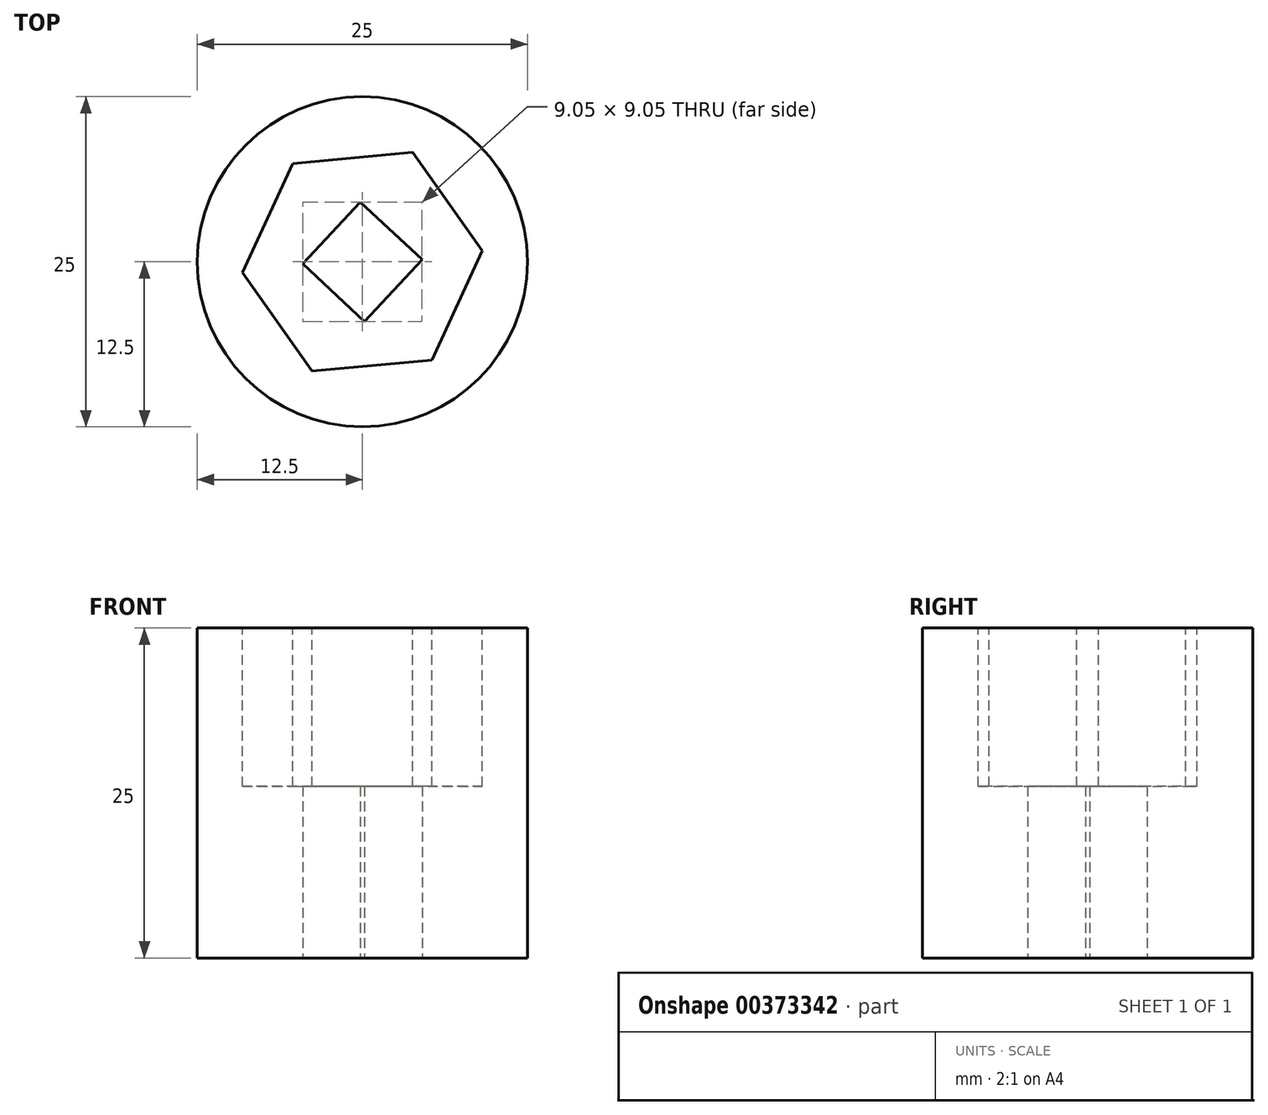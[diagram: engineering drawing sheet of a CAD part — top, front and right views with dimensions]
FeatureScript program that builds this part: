
annotation { "Feature Type Name" : "Feature", "Feature Type Description" : "" }
export const myFeature = defineFeature(function(context is Context, id is Id, definition is map)
    precondition{}
    {
        {
            var Q0;
            Q0=qCreatedBy(makeId("Top.planeOp"),FACE);
            var sketch = newSketch(context, id + "F0", { "sketchPlane" : qUnion([Q0])});
            skCircle(sketch, "E0", {"center": v(0, 0) * mm, "radius": 12.5 * mm});
            skSolve(sketch);
        }
        {
            var Q0;
            Q0=makeQuery(id+"F0.imprint","IMPRINT",FACE,{"disambiguationData":[TD([[makeQuery(id+"F0.imprint","IMPRINT",EDGE,{"derivedFrom":sQuery(id+"F0.wireOp",EDGE,"E0")}),1.0]])]});
            extrude(context, id + "F1", {"entities" : qUnion([Q0]), "depth" : 25 * mm});
        }
        {
            var Q0;
            Q0=makeQuery(id+"F1.opExtrude","CAP_FACE",FACE,{"disambiguationData":[OSD([sQuery(id+"F0.wireOp",EDGE,"E0")])],"isStart":false});
            var sketch = newSketch(context, id + "F2", { "sketchPlane" : qUnion([Q0])});
            skCircle(sketch, "E1.cCircle", {"center": v(0, 0) * mm, "radius": 7.9 * mm, "construction": true});
            skLineSegment(sketch, "E1.0", {"start": v(-3.82, -8.28) * mm, "end": v(-9.08, -0.83) * mm});
            skLineSegment(sketch, "E1.1", {"start": v(-9.08, -0.83) * mm, "end": v(-5.26, 7.45) * mm});
            skLineSegment(sketch, "E1.2", {"start": v(-5.26, 7.45) * mm, "end": v(3.82, 8.28) * mm});
            skLineSegment(sketch, "E1.3", {"start": v(3.82, 8.28) * mm, "end": v(9.08, 0.83) * mm});
            skLineSegment(sketch, "E1.4", {"start": v(9.08, 0.83) * mm, "end": v(5.26, -7.45) * mm});
            skLineSegment(sketch, "E1.5", {"start": v(5.26, -7.45) * mm, "end": v(-3.82, -8.28) * mm});
            skPoint(sketch, "E1.0.midPoint", {"position": v(-6.45, -4.56) * mm});
            skSolve(sketch);
        }
        {
            var Q0;
            Q0 = qSketchRegion(id + "F2", true);
            extrude(context, id + "F3", {"entities" : qUnion([Q0]), "operationType" : NewBodyOperationType.REMOVE, "oppositeDirection" : true, "depth" : 12 * mm});
        }
        {
            var Q0;
            Q0=makeQuery(id+"F1.opExtrude","CAP_FACE",FACE,{"disambiguationData":[OSD([sQuery(id+"F0.wireOp",EDGE,"E0")])],"isStart":true});
            var sketch = newSketch(context, id + "F4", { "sketchPlane" : qUnion([Q0])});
            skCircle(sketch, "E2.cCircle", {"center": v(0, 0) * mm, "radius": 3.2 * mm, "construction": true});
            skLineSegment(sketch, "E2.0", {"start": v(-4.52, 0.16) * mm, "end": v(0.16, 4.52) * mm});
            skLineSegment(sketch, "E2.1", {"start": v(0.16, 4.52) * mm, "end": v(4.52, -0.16) * mm});
            skLineSegment(sketch, "E2.2", {"start": v(4.52, -0.16) * mm, "end": v(-0.16, -4.52) * mm});
            skLineSegment(sketch, "E2.3", {"start": v(-0.16, -4.52) * mm, "end": v(-4.52, 0.16) * mm});
            skPoint(sketch, "E2.0.midPoint", {"position": v(-2.18, 2.34) * mm});
            skSolve(sketch);
        }
        {
            var Q0;
            Q0=makeQuery(id+"F4.imprint","IMPRINT",FACE,{"disambiguationData":[TD([[makeQuery(id+"F4.imprint","IMPRINT",EDGE,{"derivedFrom":sQuery(id+"F4.wireOp",EDGE,"E2.0")}),-1.0]])]});
            extrude(context, id + "F5", {"entities" : qUnion([Q0]), "operationType" : NewBodyOperationType.REMOVE, "oppositeDirection" : true, "depth" : 25 * mm});
        }
    });
